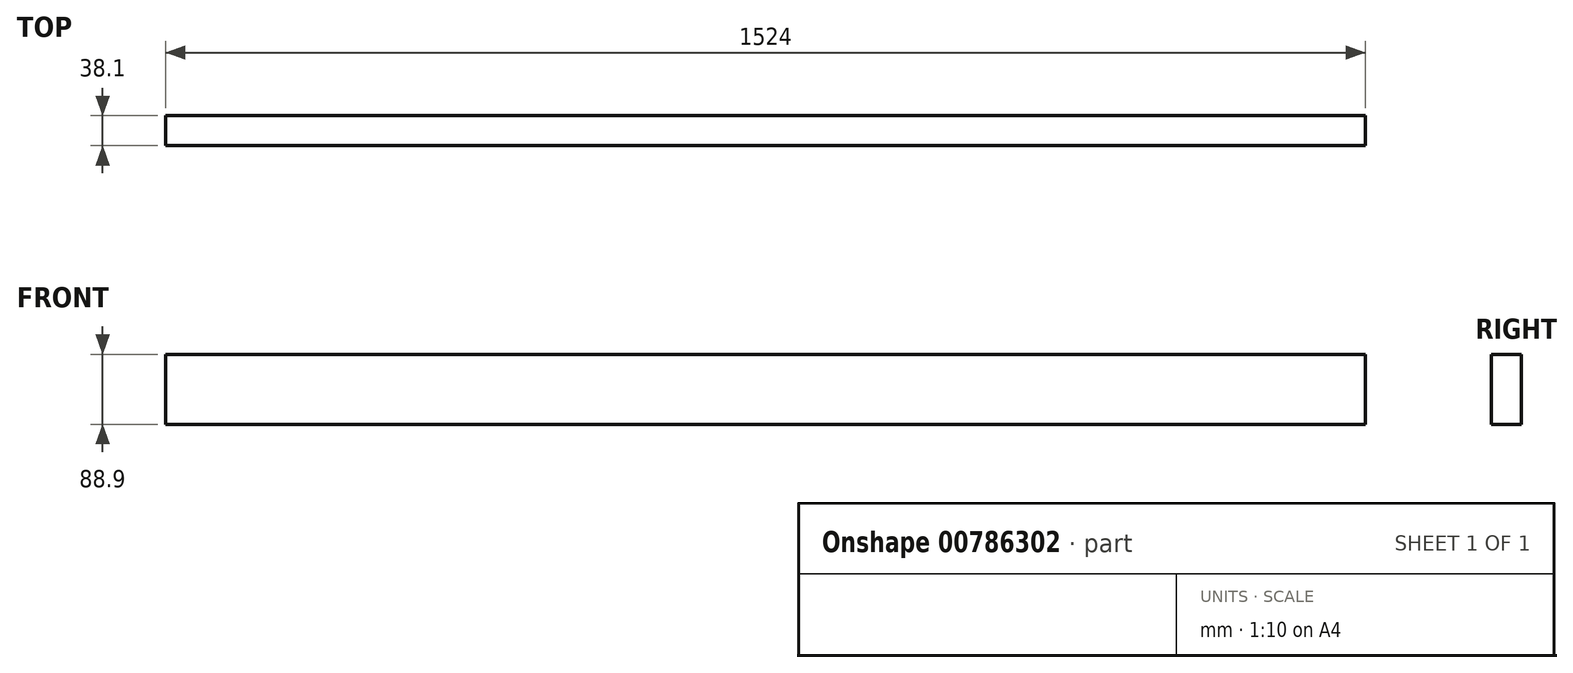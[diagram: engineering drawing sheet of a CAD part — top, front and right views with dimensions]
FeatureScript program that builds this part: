
annotation { "Feature Type Name" : "Feature", "Feature Type Description" : "" }
export const myFeature = defineFeature(function(context is Context, id is Id, definition is map)
    precondition{}
    {
        {
            var Q0;
            Q0=qCreatedBy(makeId("Front.planeOp"),FACE);
            var sketch = newSketch(context, id + "F0", { "sketchPlane" : qUnion([Q0])});
            skLineSegment(sketch, "E0.bottom", {"start": v(-762, 44.45) * mm, "end": v(762, 44.45) * mm});
            skLineSegment(sketch, "E0.top", {"start": v(-762, -44.45) * mm, "end": v(762, -44.45) * mm});
            skLineSegment(sketch, "E0.left", {"start": v(-762, 44.45) * mm, "end": v(-762, -44.45) * mm});
            skLineSegment(sketch, "E0.right", {"start": v(762, 44.45) * mm, "end": v(762, -44.45) * mm});
            skPoint(sketch, "E0.middle", {"position": v(0, 0) * mm});
            skSolve(sketch);
        }
        {
            var Q0;
            Q0=makeQuery(id+"F0.imprint","IMPRINT",FACE,{"disambiguationData":[TD([[makeQuery(id+"F0.imprint","IMPRINT",EDGE,{"derivedFrom":sQuery(id+"F0.wireOp",EDGE,"E0.bottom")}),-1.0]])]});
            extrude(context, id + "F1", {"entities" : qUnion([Q0]), "endBound" : BoundingType.SYMMETRIC, "depth" : 38.1 * mm, "offsetDistance" : 25.4 * mm});
        }
    });
